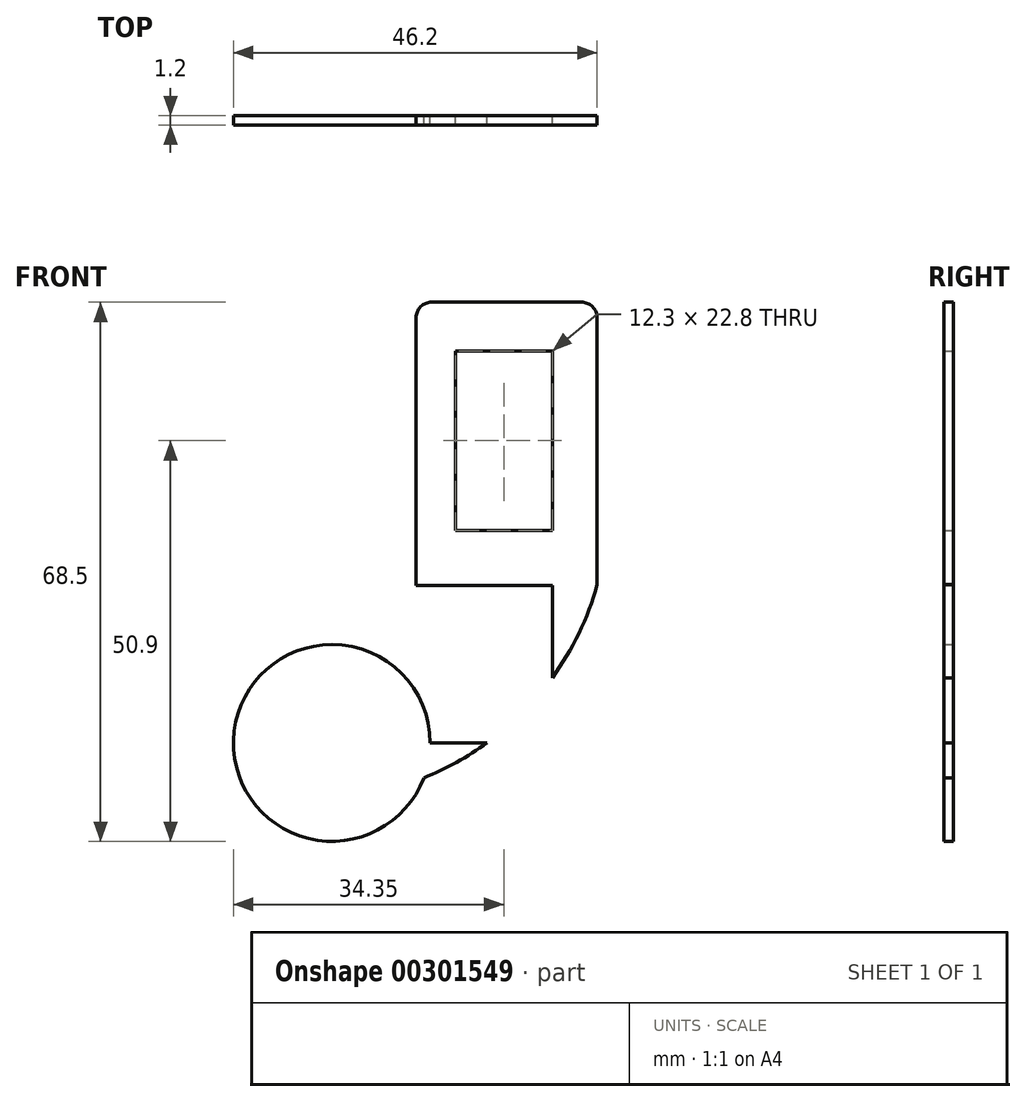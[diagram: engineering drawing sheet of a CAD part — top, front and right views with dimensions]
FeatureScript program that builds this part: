
annotation { "Feature Type Name" : "Feature", "Feature Type Description" : "" }
export const myFeature = defineFeature(function(context is Context, id is Id, definition is map)
    precondition{}
    {
        {
            var Q0;
            Q0=qCreatedBy(makeId("Front.planeOp"),FACE);
            var sketch = newSketch(context, id + "F0", { "sketchPlane" : qUnion([Q0])});
            skCircle(sketch, "E0", {"center": v(-28, 0) * mm, "radius": 12.5 * mm});
            skLineSegment(sketch, "E1", {"start": v(-28, 0) * mm, "end": v(0, 0) * mm});
            skLineSegment(sketch, "E2", {"start": v(0, 0) * mm, "end": v(0, 28) * mm});
            skLineSegment(sketch, "E3.bottom", {"start": v(-30, 30) * mm, "end": v(0, 30) * mm, "construction": true});
            skLineSegment(sketch, "E3.top", {"start": v(-30, 0) * mm, "end": v(0, 0) * mm, "construction": true});
            skLineSegment(sketch, "E3.left", {"start": v(-30, 30) * mm, "end": v(-30, 0) * mm, "construction": true});
            skLineSegment(sketch, "E3.right", {"start": v(0, 30) * mm, "end": v(0, 0) * mm, "construction": true});
            skArc(sketch, "E4", {"start": v(-16.3, -4.42) * mm, "mid": v(-2.42, 5.27) * mm, "end": v(5.7, 20.11) * mm});
            skLineSegment(sketch, "E5.bottom", {"start": v(-17.3, 20) * mm, "end": v(5.7, 20) * mm});
            skLineSegment(sketch, "E5.top", {"start": v(-15.3, 56) * mm, "end": v(3.7, 56) * mm});
            skLineSegment(sketch, "E5.left", {"start": v(-17.3, 20) * mm, "end": v(-17.3, 54) * mm});
            skLineSegment(sketch, "E5.right", {"start": v(5.7, 20) * mm, "end": v(5.7, 54) * mm});
            skPoint(sketch, "E6.visualSharp", {"position": v(-17.3, 56) * mm});
            skArc(sketch, "E6.filletArc", {"start": v(-15.3, 56) * mm, "mid": v(-16.71, 55.41) * mm, "end": v(-17.3, 54) * mm});
            skPoint(sketch, "E7.visualSharp", {"position": v(5.7, 56) * mm});
            skArc(sketch, "E7.filletArc", {"start": v(5.7, 54) * mm, "mid": v(5.11, 55.41) * mm, "end": v(3.7, 56) * mm});
            skLineSegment(sketch, "E8.bottom", {"start": v(-12.3, 27) * mm, "end": v(0, 27) * mm});
            skLineSegment(sketch, "E8.top", {"start": v(-12.3, 49.8) * mm, "end": v(0, 49.8) * mm});
            skLineSegment(sketch, "E8.left", {"start": v(-12.3, 27) * mm, "end": v(-12.3, 49.8) * mm});
            skLineSegment(sketch, "E8.right", {"start": v(0, 27) * mm, "end": v(0, 49.8) * mm});
            skArc(sketch, "E9", {"start": v(-28, 12.5) * mm, "mid": v(-21.46, 14.55) * mm, "end": v(-17.3, 20) * mm});
            skSolve(sketch);
        }
        {
            var Q0;
            {var subQ4=sQuery(id+"F0.wireOp",EDGE,"E0");var subQ5=makeQuery(id+"F0.imprint","INTERSECT",VERTEX,{"derivedFrom":[subQ4,sQuery(id+"F0.wireOp",EDGE,"E4")]});Q0=makeQuery(id+"F0.imprint","IMPRINT",FACE,{"disambiguationData":[TD([[makeQuery(id+"F0.imprint","IMPRINT",EDGE,{"disambiguationData":[TD([[subQ5,1.0]])],"derivedFrom":subQ4}),1.0]])]});}
            var Q1;
            {var subQ0=sQuery(id+"F0.wireOp",EDGE,"E3.left");var subQ1=sQuery(id+"F0.wireOp",EDGE,"E0");var subQ2=makeQuery(id+"F0.imprint","INTERSECT",VERTEX,{"derivedFrom":[subQ1,subQ0]});Q1=makeQuery(id+"F0.imprint","IMPRINT",FACE,{"disambiguationData":[TD([[makeQuery(id+"F0.imprint","IMPRINT",EDGE,{"disambiguationData":[TD([[subQ2,1.0]])],"derivedFrom":subQ1}),1.0]])]});}
            var Q2;
            {var subQ0=sQuery(id+"F0.wireOp",EDGE,"E0");var subQ1=makeQuery(id+"F0.imprint","INTERSECT",VERTEX,{"derivedFrom":[subQ0,sQuery(id+"F0.wireOp",EDGE,"uSPEjawG-pwjX-fEwL-S6gs-5jgCuuEDe3bl")]});Q2=makeQuery(id+"F0.imprint","IMPRINT",FACE,{"disambiguationData":[TD([[makeQuery(id+"F0.imprint","IMPRINT",EDGE,{"disambiguationData":[TD([[subQ1,1.0]])],"derivedFrom":subQ0}),1.0]])]});}
            var Q3;
            {var subQ5=sQuery(id+"F0.wireOp",EDGE,"uSPEjawG-pwjX-fEwL-S6gs-5jgCuuEDe3bl");Q3=makeQuery(id+"F0.imprint","IMPRINT",FACE,{"disambiguationData":[TD([[makeQuery(id+"F0.imprint","IMPRINT",EDGE,{"derivedFrom":subQ5}),-1.0]])]});}
            var Q4;
            {var subQ0=sQuery(id+"F0.wireOp",EDGE,"zumYEtJS-4euV-DDxV-KFL1-Nszc64kHzFny");var subQ1=makeQuery(id+"F0.imprint","INTERSECT",VERTEX,{"derivedFrom":[subQ0,sQuery(id+"F0.wireOp",EDGE,"uSPEjawG-pwjX-fEwL-S6gs-5jgCuuEDe3bl")]});Q4=makeQuery(id+"F0.imprint","IMPRINT",FACE,{"disambiguationData":[TD([[makeQuery(id+"F0.imprint","IMPRINT",EDGE,{"disambiguationData":[TD([[subQ1,1.0]])],"derivedFrom":subQ0}),1.0]])]});}
            var Q5;
            {var subQ0=sQuery(id+"F0.wireOp",EDGE,"E3.bottom");var subQ1=sQuery(id+"F0.wireOp",EDGE,"zumYEtJS-4euV-DDxV-KFL1-Nszc64kHzFny");var subQ2=makeQuery(id+"F0.imprint","INTERSECT",VERTEX,{"derivedFrom":[subQ1,subQ0]});Q5=makeQuery(id+"F0.imprint","IMPRINT",FACE,{"disambiguationData":[TD([[makeQuery(id+"F0.imprint","IMPRINT",EDGE,{"disambiguationData":[TD([[subQ2,-1.0]])],"derivedFrom":subQ1}),1.0]])]});}
            var Q6;
            {var subQ3=sQuery(id+"F0.wireOp",EDGE,"zumYEtJS-4euV-DDxV-KFL1-Nszc64kHzFny");var subQ5=makeQuery(id+"F0.imprint","INTERSECT",VERTEX,{"derivedFrom":[subQ3,sQuery(id+"F0.wireOp",EDGE,"E4")]});Q6=makeQuery(id+"F0.imprint","IMPRINT",FACE,{"disambiguationData":[TD([[makeQuery(id+"F0.imprint","IMPRINT",EDGE,{"disambiguationData":[TD([[subQ5,1.0]])],"derivedFrom":subQ3}),1.0]])]});}
            var Q7;
            {var subQ0=sQuery(id+"F0.wireOp",EDGE,"E4");var subQ1=sQuery(id+"F0.wireOp",EDGE,"zumYEtJS-4euV-DDxV-KFL1-Nszc64kHzFny");var subQ2=makeQuery(id+"F0.imprint","INTERSECT",VERTEX,{"derivedFrom":[subQ1,subQ0]});Q7=makeQuery(id+"F0.imprint","IMPRINT",FACE,{"disambiguationData":[TD([[makeQuery(id+"F0.imprint","IMPRINT",EDGE,{"disambiguationData":[TD([[subQ2,1.0]])],"derivedFrom":subQ1}),-1.0]])]});}
            var Q8;
            {var subQ0=sQuery(id+"F0.wireOp",EDGE,"E4");var subQ1=sQuery(id+"F0.wireOp",EDGE,"E0");var subQ2=makeQuery(id+"F0.imprint","INTERSECT",VERTEX,{"derivedFrom":[subQ1,subQ0]});Q8=makeQuery(id+"F0.imprint","IMPRINT",FACE,{"disambiguationData":[TD([[makeQuery(id+"F0.imprint","IMPRINT",EDGE,{"disambiguationData":[TD([[subQ2,-1.0]])],"derivedFrom":subQ1}),-1.0]])]});}
            var Q9;
            {var subQ4=sQuery(id+"F0.wireOp",EDGE,"E8.bottom");Q9=makeQuery(id+"F0.imprint","IMPRINT",FACE,{"disambiguationData":[TD([[makeQuery(id+"F0.imprint","IMPRINT",EDGE,{"derivedFrom":subQ4}),-1.0]])]});}
            var Q10;
            {var subQ9=sQuery(id+"F0.wireOp",EDGE,"E8.top");Q10=makeQuery(id+"F0.imprint","IMPRINT",FACE,{"disambiguationData":[TD([[makeQuery(id+"F0.imprint","IMPRINT",EDGE,{"derivedFrom":subQ9}),1.0]])]});}
            var Q11;
            {var subQ8=sQuery(id+"F0.wireOp",EDGE,"E5.top");Q11=makeQuery(id+"F0.imprint","IMPRINT",FACE,{"disambiguationData":[TD([[makeQuery(id+"F0.imprint","IMPRINT",EDGE,{"derivedFrom":subQ8}),-1.0]])]});}
            var Q12;
            {var subQ0=sQuery(id+"F0.wireOp",EDGE,"E4");var subQ1=sQuery(id+"F0.wireOp",EDGE,"E3.right");var subQ2=makeQuery(id+"F0.imprint","INTERSECT",VERTEX,{"derivedFrom":[subQ1,subQ0]});Q12=makeQuery(id+"F0.imprint","IMPRINT",FACE,{"disambiguationData":[TD([[makeQuery(id+"F0.imprint","IMPRINT",EDGE,{"disambiguationData":[TD([[subQ2,1.0]])],"derivedFrom":subQ1}),1.0]])]});}
            var Q13;
            {var subQ0=sQuery(id+"F0.wireOp",EDGE,"E5.left");var subQ1=sQuery(id+"F0.wireOp",EDGE,"A5wlopPC-ItDW-nRQ4-Ny0s-uAsfGBsNxhSs");var subQ2=makeQuery(id+"F0.imprint","INTERSECT",VERTEX,{"derivedFrom":[subQ1,subQ0]});Q13=makeQuery(id+"F0.imprint","IMPRINT",FACE,{"disambiguationData":[TD([[makeQuery(id+"F0.imprint","IMPRINT",EDGE,{"disambiguationData":[TD([[subQ2,-1.0]])],"derivedFrom":subQ1}),1.0]])]});}
            var Q14;
            {var subQ0=sQuery(id+"F0.wireOp",EDGE,"vYFbtE1S-u3IN-aoDM-TaCb-u6LQwpx6xxUC");var subQ3=sQuery(id+"F0.wireOp",EDGE,"E3.top");var subQ5=makeQuery(id+"F0.imprint","INTERSECT",VERTEX,{"derivedFrom":[subQ0,subQ3]});Q14=makeQuery(id+"F0.imprint","IMPRINT",FACE,{"disambiguationData":[TD([[makeQuery(id+"F0.imprint","IMPRINT",EDGE,{"disambiguationData":[TD([[subQ5,-1.0]])],"derivedFrom":subQ3}),1.0]])]});}
            var Q15;
            {var subQ5=sQuery(id+"F0.wireOp",EDGE,"LoDQbfpj-PH9O-zxvZ-Qv1Z-xV6kipDemV7K");Q15=makeQuery(id+"F0.imprint","IMPRINT",FACE,{"disambiguationData":[TD([[makeQuery(id+"F0.imprint","IMPRINT",EDGE,{"derivedFrom":subQ5}),-1.0]])]});}
            var Q16;
            {var subQ0=sQuery(id+"F0.wireOp",EDGE,"E4");var subQ1=sQuery(id+"F0.wireOp",EDGE,"E2");var subQ2=makeQuery(id+"F0.imprint","INTERSECT",VERTEX,{"derivedFrom":[subQ1,subQ0]});Q16=makeQuery(id+"F0.imprint","IMPRINT",FACE,{"disambiguationData":[TD([[makeQuery(id+"F0.imprint","IMPRINT",EDGE,{"disambiguationData":[TD([[subQ2,-1.0]])],"derivedFrom":subQ1}),-1.0]])]});}
            var Q17;
            {var subQ7=sQuery(id+"F0.wireOp",EDGE,"E0");var subQ9=sQuery(id+"F0.wireOp",EDGE,"E9");var subQ10=makeQuery(id+"F0.imprint","INTERSECT",VERTEX,{"disambiguationData":[OD(1.0)],"derivedFrom":[subQ7,subQ9]});Q17=makeQuery(id+"F0.imprint","IMPRINT",FACE,{"disambiguationData":[TD([[makeQuery(id+"F0.imprint","IMPRINT",EDGE,{"disambiguationData":[TD([[subQ10,1.0]])],"derivedFrom":subQ7}),-1.0]])]});}
            extrude(context, id + "F1", {"entities" : qUnion([Q0, Q1, Q2, Q3, Q4, Q5, Q6, Q7, Q8, Q9, Q10, Q11, Q12, Q13, Q14, Q15, Q16, Q17]), "depth" : 1.2 * mm});
        }
    });
